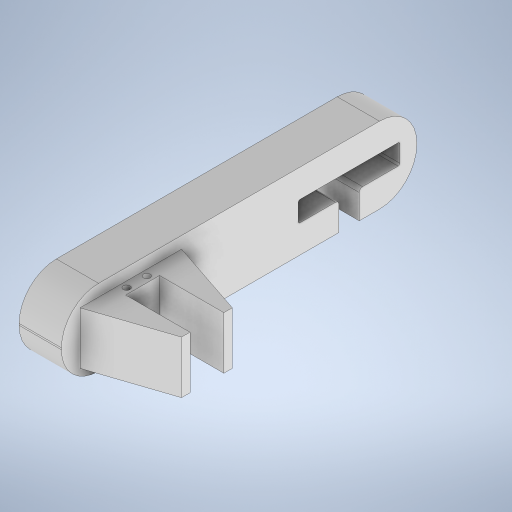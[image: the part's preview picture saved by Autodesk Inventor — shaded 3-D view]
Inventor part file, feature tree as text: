
AUTODESK INVENTOR PART (.ipt)
format: ipt  version: 2023 (Build 270158000, 158)  size: 303,104 bytes
history: native  units: mm
features: extrude x4, sketch x4, fillet x3, other x1
ambient origin geometry x8: Origin, YZ Plane, XZ Plane, XY Plane, X Axis, Y Axis, Z Axis, Center Point
bodies: Body1 (feature_tree)
feature tree (12):
  other  "實體1"
  extrude  "擠出1"  Depth=210.0mm
  fillet  "圓角1"  Radius=45.0mm
  extrude  "擠出2"  Depth=25.0mm TaperAngle=0.0deg
  fillet  "圓角2"  Radius=22.0mm
  fillet  "圓角3"  Radius=12.0mm
  extrude  "擠出3"  Depth=60.0mm
  extrude  "擠出4"  Depth=12.0mm
  sketch  "草圖1"
  sketch  "草圖2"
  sketch  "草圖3"
  sketch  "草圖4"
